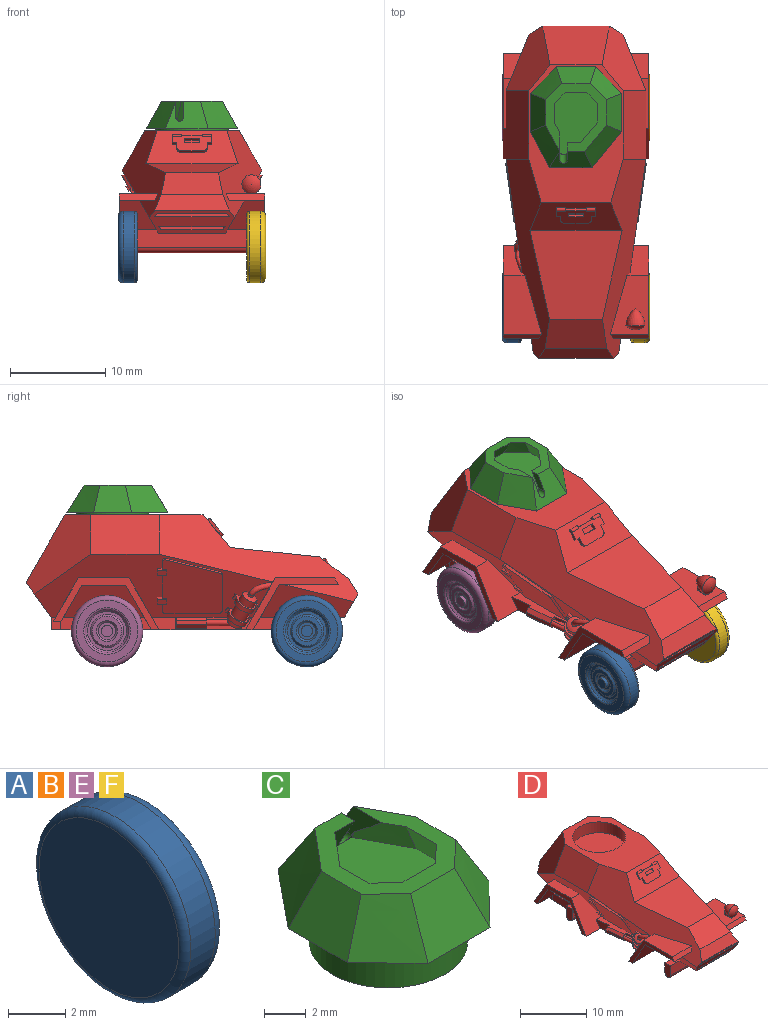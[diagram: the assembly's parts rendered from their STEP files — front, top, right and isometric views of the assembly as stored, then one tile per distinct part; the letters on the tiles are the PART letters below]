
ASSEMBLY  parts=6 mates=5
PART A: 14 faces, bbox 2x8.1x8.1 mm
  f0: cone r=1.75mm half-angle=45deg, axis (-1,0,0), area 2.9mm2, adj f1,f13
  f1: plane 3.1x3.1mm, normal (1,0,0), area 3.7mm2, adj f0,f2
  f2: cone r=0.9mm half-angle=45deg, axis (1,0,0), area 1.8mm2, adj f1,f3
  f3: plane 1.8x1.8mm, normal (1,0,0), area 1.4mm2, adj f2,f4
  f4: cylinder r=0.6mm len=1.2mm, axis (-1,0,0), area 1.5mm2, adj f3,f5
  f5: plane 1.2x1.2mm, normal (1,0,0), area 1.1mm2, adj f4
  f6: plane 6.9x6.9mm, normal (-1,0,0), area 37.4mm2, adj f7
  f7: torus R=3.45mm, axis (-1,0,0), area 10.8mm2, adj f6,f8
  f8: cylinder r=3.75mm len=7.5mm, axis (-1,0,0), area 28.3mm2, adj f7,f9
  f9: torus R=3.25mm, axis (-1,0,0), area 17.6mm2, adj f8,f10
  f10: plane 6.5x6.5mm, normal (1,0,0), area 14.3mm2, adj f9,f11
  f11: torus R=2.45mm, axis (-1,0,0), area 4.6mm2, adj f10,f12
  f12: cone r=2.25mm half-angle=45deg, axis (1,0,0), area 3.8mm2, adj f11,f13
  f13: plane 4.1x4.1mm, normal (1,0,0), area 3.6mm2, adj f0,f12
PART B: same geometry as A
PART C: 25 faces, bbox 11.2x12.2x7.1 mm
  f0: plane 4.5x2.9mm, normal (0,0.86,0.51), area 10.1mm2, adj f3,f4,f7,f8,f20,f21,f22
  f1: plane 0.63x0.61mm, normal (0,-0.86,-0.51), area 0.1mm2, adj f12,f15,f20,f22
  f2: plane 2.35x2.11mm, normal (0,-0.86,-0.51), area 4.1mm2, adj f4,f12,f16,f21,f22
  f3: plane 10.6x9.6mm, normal (0,0,-1), area 39.1mm2, adj f0,f5,f6,f7,f8,f9,f10,f11
  f4: plane 7.1x6.4mm, normal (0,0,1), area 16.9mm2, adj f0,f2,f5,f6,f7,f8,f9,f10
  f5: bspline ~3.54x3.39mm, area 10.4mm2, adj f3,f4,f6,f11
  f6: plane 4x2.9mm, normal (0.88,0,0.48), area 11.1mm2, adj f3,f4,f5,f7
  f7: bspline ~4.55x3.33mm, area 12.6mm2, adj f0,f3,f4,f6
  f8: bspline ~4.54x4.02mm, area 14.2mm2, adj f0,f3,f4,f9
  f9: plane 4x2.9mm, normal (-0.88,0,0.48), area 11.1mm2, adj f3,f4,f8,f10
  f10: bspline ~3.54x3.39mm, area 10.4mm2, adj f3,f4,f9,f11
  f11: plane 4.2x2.9mm, normal (0,-0.85,0.53), area 12.3mm2, adj f3,f4,f5,f10
  f12: plane 7.77x6.89mm, normal (0,0,1), area 44.2mm2, adj f1,f2,f13,f14,f15,f16,f17,f18
  f13: offset ~5.14x4.99mm, area 5.1mm2, adj f4,f12,f14,f19
  f14: plane 3.04x2.13mm, normal (-0.88,0,-0.48), area 6.1mm2, adj f4,f12,f13,f15
  f15: offset ~6.15x4.93mm, area 5.8mm2, adj f1,f4,f12,f14,f20
  f16: offset ~6.14x5.62mm, area 8mm2, adj f2,f4,f12,f17
  f17: plane 2.96x2.13mm, normal (0.88,0,-0.48), area 5.9mm2, adj f4,f12,f16,f18
  f18: offset ~5.14x4.99mm, area 5.1mm2, adj f4,f12,f17,f19
  f19: plane 3.14x2.12mm, normal (0,0.85,-0.53), area 6.7mm2, adj f4,f12,f13,f18
  f20: plane 2.95x1.7mm, normal (-1,0,0), area 2.3mm2, adj f0,f1,f4,f15,f22
  f21: plane 1.92x1.7mm, normal (1,0,0), area 1.6mm2, adj f0,f2,f4,f22
  f22: cylinder r=0.4mm len=1.16mm, axis (0,1,0), area 1.2mm2, adj f0,f1,f2,f20,f21
  f23: cylinder r=3.8mm len=7.6mm, axis (0,0,1), area 52.5mm2, adj f3,f24
  f24: plane 7.6x7.6mm, normal (0,0,-1), area 45.4mm2, adj f23
PART D: 210 faces, bbox 15.4x35x12.9 mm
  f0: plane 10.64x1.33mm, normal (-0.99,-0.11,0), area 5.7mm2, adj f1,f2,f5,f14,f104,f109,f137,f177
  f1: cylinder r=0.86mm len=1.76mm, axis (0.45,0.45,-0.77), area 2.1mm2, adj f0,f2,f3,f6,f137,f172,f178,f198
  f2: plane 1.59x1.31mm, normal (0.45,0.45,-0.77), area 0.9mm2, adj f0,f1,f198,f199,f201
  f3: plane 25.09x6.62mm, normal (-0.87,0,-0.5), area 73.1mm2, adj f1,f4,f5,f32,f95,f99,f100,f101
  f4: cylinder r=0.86mm len=2.12mm, axis (0.45,0.45,-0.77), area 6.7mm2, adj f3,f177,f186
  f5: plane 0.33x0.04mm, normal (0,0,1), area 0mm2, adj f0,f3,f177
  f6: plane 2.66x0.3mm, normal (-0.99,-0.11,0), area 0.7mm2, adj f1,f137,f172,f196,f200
  f7: plane 6.2x4.05mm, normal (0,0,1), area 18.4mm2, adj f25,f36,f37,f38,f165,f166,f167,f168
  f8: plane 9.67x3.45mm, normal (0,-0.77,0.64), area 30.3mm2, adj f9,f25,f26,f27,f99,f144,f145,f146
  f9: plane 2.2x0.23mm, normal (0,0.64,0.77), area 0.7mm2, adj f8,f157,f160,f161
  f10: plane 9.16x5.26mm, normal (0,0,-1), area 47.4mm2, adj f12,f64,f68,f86,f90,f133
  f11: plane 3.98x1.04mm, normal (0,0,1), area 3.9mm2, adj f12,f18,f22,f86
  f12: plane 4.25x1.33mm, normal (1,0.03,0), area 5.6mm2, adj f10,f11,f18,f64,f86
  f13: plane 4.28x1.47mm, normal (0,0,-1), area 5.4mm2, adj f15,f23,f34,f81
  f14: plane 19.8x15.3mm, normal (0,0,-1), area 161.2mm2, adj f0,f15,f17,f34,f36,f38,f40,f42
  f15: plane 5.05x1.33mm, normal (1,-0.1,0), area 6.2mm2, adj f13,f14,f34,f81
  f16: plane 8.96x2.43mm, normal (0,-0.87,-0.5), area 17mm2, adj f23,f24,f25,f29,f71,f72,f73,f75
  f17: plane 4.66x4.11mm, normal (0,0.87,-0.5), area 16.6mm2, adj f14,f22,f41,f42,f66,f67
  f18: plane 4.11x3.79mm, normal (0,-0.87,-0.5), area 13.8mm2, adj f11,f12,f20,f22,f41,f42
  f19: plane 4.59x4.11mm, normal (0,0.87,0.5), area 15.6mm2, adj f20,f21,f39,f42,f64,f65
  f20: plane 3.2x0.8mm, normal (0,0,-1), area 2.6mm2, adj f18,f19,f42,f64
  f21: plane 25.07x6.6mm, normal (0.87,0,-0.5), area 76.5mm2, adj f19,f25,f30,f32,f33,f36,f39,f40
  f22: plane 8.46x3.33mm, normal (0.87,0,-0.5), area 24.7mm2, adj f11,f17,f18,f41,f66,f84,f85,f86
  f23: plane 9.79x3.43mm, normal (0.87,0,-0.5), area 25.8mm2, adj f13,f16,f24,f25,f34,f35,f79,f80
  f24: plane 7.08x3.37mm, normal (0,0,-1), area 23.9mm2, adj f16,f23,f79,f98
  f25: plane 20.88x9.13mm, normal (0.84,-0.24,0.49), area 81.9mm2, adj f7,f8,f16,f21,f23,f26,f27,f28
  f26: plane 14.5x9.9mm, normal (0,0,1), area 81.4mm2, adj f8,f25,f30,f31,f33,f99,f100,f101
  f27: plane 9.67x9.35mm, normal (0,-0.1,0.99), area 71.5mm2, adj f8,f25,f28,f99
  f28: plane 6.49x3.04mm, normal (0,-0.6,0.8), area 22.9mm2, adj f25,f27,f29,f99
  f29: plane 7.78x1.61mm, normal (0,-0.85,0.53), area 13.6mm2, adj f16,f25,f28,f99
  f30: plane 7.2x4.16mm, normal (0.87,0,0.5), area 34.6mm2, adj f21,f25,f26,f33
  f31: plane 7.1x6.99mm, normal (0,0.87,0.5), area 51.2mm2, adj f26,f32,f33,f101
  f32: plane 9.88x3.65mm, normal (0,0.81,-0.59), area 38.2mm2, adj f3,f21,f31,f33,f68,f101
  f33: plane 8.33x6.8mm, normal (0.71,0.58,0.41), area 41.3mm2, adj f21,f26,f30,f31,f32
  f34: plane 5.15x4.76mm, normal (0,-0.87,-0.5), area 20.2mm2, adj f13,f14,f15,f23,f35,f38
  f35: plane 6.2x3.76mm, normal (0,0,-1), area 17.9mm2, adj f23,f25,f34,f37,f38
  f36: plane 5.46x4.11mm, normal (0,0.87,0.5), area 20.3mm2, adj f7,f14,f21,f25,f38,f70
  f37: plane 4.05x0.69mm, normal (0,-0.87,0.5), area 3.1mm2, adj f7,f25,f35,f38
  f38: plane 9.75x5.46mm, normal (1,0,0), area 8.4mm2, adj f7,f14,f34,f35,f36,f37
  f39: plane 5.3x1.73mm, normal (0,0,1), area 9.1mm2, adj f19,f21,f40,f42
  f40: plane 5.46x4.11mm, normal (0,-0.87,0.5), area 18.4mm2, adj f14,f21,f39,f42,f69,f70
  f41: plane 4.62x2.19mm, normal (0,0,-1), area 10.1mm2, adj f17,f18,f22,f42
  f42: plane 11.1x5.46mm, normal (1,0,0), area 11.4mm2, adj f14,f17,f18,f19,f20,f39,f40,f41
  f43: plane 2.67x1.71mm, normal (0,1,0), area 0.9mm2, adj f21,f53,f55,f60
  f44: plane 0.93x0.71mm, normal (0,1,0), area 0.3mm2, adj f21,f45,f53,f54
  f45: cylinder r=0.3mm len=0.41mm, axis (-0.87,0,0.5), area 0.2mm2, adj f21,f44,f46,f53
  f46: plane 5.7x1.54mm, normal (0.48,-0.27,0.83), area 1.8mm2, adj f21,f45,f47,f53
  f47: cylinder r=0.3mm len=0.4mm, axis (-0.87,0,0.5), area 0.1mm2, adj f21,f46,f48,f53
  f48: plane 3.88x2.41mm, normal (0,-1,0), area 1.3mm2, adj f21,f47,f49,f53
  f49: cylinder r=0.3mm len=0.41mm, axis (-0.87,0,0.5), area 0.1mm2, adj f21,f48,f50,f53
  f50: plane 5.7x0.26mm, normal (-0.5,0,-0.87), area 1.7mm2, adj f21,f49,f51,f53
  f51: cylinder r=0.3mm len=0.41mm, axis (-0.87,0,0.5), area 0.1mm2, adj f21,f50,f52,f53
  f52: plane 0.93x0.71mm, normal (0,1,0), area 0.3mm2, adj f21,f51,f53,f59
  f53: plane 6.3x5.63mm, normal (0.87,0,-0.5), area 35.3mm2, adj f43,f44,f45,f46,f47,f48,f49,f50
  f54: plane 1x0.43mm, normal (0.5,0,0.87), area 0.4mm2, adj f21,f44,f53,f56,f57,f58
  f55: plane 1x0.43mm, normal (-0.5,0,-0.87), area 0.4mm2, adj f21,f43,f53,f56,f57,f58
  f56: plane 0.62x0.47mm, normal (0,-1,0), area 0.1mm2, adj f53,f54,f55,f58
  f57: plane 0.77x0.73mm, normal (0,1,0), area 0.3mm2, adj f21,f54,f55,f58
  f58: plane 1x0.52mm, normal (0.87,0,-0.5), area 0.6mm2, adj f54,f55,f56,f57
  f59: plane 1x0.43mm, normal (-0.5,0,-0.87), area 0.3mm2, adj f21,f52,f53,f61,f62,f63
  f60: plane 1x0.43mm, normal (0.5,0,0.87), area 0.3mm2, adj f21,f43,f53,f61,f62,f63
  f61: plane 0.77x0.73mm, normal (0,1,0), area 0.3mm2, adj f21,f59,f60,f63
  f62: plane 0.62x0.47mm, normal (0,-1,0), area 0.1mm2, adj f53,f59,f60,f63
  f63: plane 1x0.52mm, normal (0.87,0,-0.5), area 0.6mm2, adj f59,f60,f61,f62
  f64: plane 1.33x1.01mm, normal (1,0,0), area 1mm2, adj f10,f12,f19,f20,f65,f68
  f65: plane 0.91x0.48mm, normal (0,0,1), area 0.4mm2, adj f19,f21,f64,f68
  f66: plane 3.28x1.18mm, normal (0,0,1), area 3.7mm2, adj f17,f22,f67,f85
  f67: plane 4.05x1.33mm, normal (1,0.03,0), area 4.9mm2, adj f14,f17,f66,f85
  f68: plane 8.9x1.33mm, normal (0,1,0), area 11.8mm2, adj f10,f32,f64,f65,f133,f134
  f69: plane 10.64x1.2mm, normal (0,0,1), area 6.4mm2, adj f21,f40,f70
  f70: plane 10.64x1.33mm, normal (0.99,-0.11,0), area 13.2mm2, adj f14,f36,f40,f69
  f71: plane 6.59x0.52mm, normal (0,-0.5,0.87), area 4mm2, adj f16,f72,f74,f138
  f72: plane 0.72x0.65mm, normal (-0.89,-0.22,0.39), area 0.3mm2, adj f16,f71,f73,f74
  f73: plane 6.99x0.52mm, normal (0,0.5,-0.87), area 4.2mm2, adj f16,f72,f74,f138
  f74: plane 6.99x0.35mm, normal (0,-0.87,-0.5), area 2.7mm2, adj f71,f72,f73,f138
  f75: plane 0.72x0.65mm, normal (-0.84,0.27,-0.47), area 0.3mm2, adj f16,f76,f77,f78
  f76: plane 7.34x0.52mm, normal (0,0.5,-0.87), area 4.4mm2, adj f16,f75,f78,f139
  f77: plane 7.86x0.52mm, normal (0,-0.5,0.87), area 4.7mm2, adj f16,f75,f78,f139
  f78: plane 7.86x0.35mm, normal (0,-0.87,-0.5), area 3mm2, adj f75,f76,f77,f139
  f79: plane 11.5x1.8mm, normal (0,-1,0), area 18.3mm2, adj f23,f24,f80,f82,f83,f98,f140,f141
  f80: plane 2.02x1.2mm, normal (0,0,1), area 2.4mm2, adj f23,f79,f81,f83
  f81: plane 11.5x1.8mm, normal (0,1,0), area 12.8mm2, adj f13,f14,f15,f23,f80,f82,f83,f91
  f82: cylinder r=0.6mm len=11.5mm, axis (-1,0,0), area 21.7mm2, adj f79,f81,f83,f141
  f83: plane 2.4x1.2mm, normal (1,0,0), area 2.7mm2, adj f79,f80,f81,f82
  f84: plane 2.02x1.2mm, normal (0,0,1), area 2.4mm2, adj f22,f85,f86,f88
  f85: plane 11.5x1.8mm, normal (0,-1,0), area 6mm2, adj f14,f22,f66,f67,f84,f87,f88,f97
  f86: plane 11.5x1.8mm, normal (0,1,0), area 6.1mm2, adj f10,f11,f12,f22,f84,f87,f88,f89
  f87: cylinder r=0.6mm len=11.5mm, axis (-1,0,0), area 21.7mm2, adj f85,f86,f88,f143
  f88: plane 2.4x1.2mm, normal (1,0,0), area 2.7mm2, adj f84,f85,f86,f87
  f89: plane 3.98x1.04mm, normal (0,0,1), area 3.9mm2, adj f86,f90,f94,f97
  f90: plane 4.25x1.33mm, normal (-1,0.03,0), area 5.6mm2, adj f10,f86,f89,f94,f133
  f91: plane 4.28x1.47mm, normal (0,0,-1), area 5.4mm2, adj f81,f92,f98,f102
  f92: plane 5.05x1.33mm, normal (-1,-0.1,0), area 6.2mm2, adj f14,f81,f91,f102
  f93: plane 4.66x4.11mm, normal (0,0.87,-0.5), area 16.6mm2, adj f14,f97,f110,f111,f135,f136
  f94: plane 4.11x3.79mm, normal (0,-0.87,-0.5), area 13.8mm2, adj f89,f90,f96,f97,f110,f111
  f95: plane 4.59x4.11mm, normal (0,0.87,0.5), area 15.6mm2, adj f3,f96,f108,f111,f133,f134
  f96: plane 3.2x0.8mm, normal (0,0,-1), area 2.6mm2, adj f94,f95,f111,f133
  f97: plane 8.46x3.33mm, normal (-0.87,0,-0.5), area 24.7mm2, adj f85,f86,f89,f93,f94,f110,f135,f142
  f98: plane 9.79x3.43mm, normal (-0.87,0,-0.5), area 25.8mm2, adj f16,f24,f79,f81,f91,f99,f102,f103
  f99: plane 20.88x9.13mm, normal (-0.84,-0.24,0.49), area 81.9mm2, adj f3,f8,f16,f26,f27,f28,f29,f98
  f100: plane 7.2x4.16mm, normal (-0.87,0,0.5), area 34.6mm2, adj f3,f26,f99,f101
  f101: plane 8.33x6.8mm, normal (-0.71,0.58,0.41), area 41.3mm2, adj f3,f26,f31,f32,f100
  f102: plane 5.15x4.76mm, normal (0,-0.87,-0.5), area 20.2mm2, adj f14,f91,f92,f98,f103,f107
  f103: plane 6.2x3.76mm, normal (0,0,-1), area 17.9mm2, adj f98,f99,f102,f105,f107
  f104: plane 5.49x4.14mm, normal (0,0.87,0.5), area 20.1mm2, adj f0,f3,f14,f99,f106,f107,f192,f193
  f105: plane 4.05x0.69mm, normal (0,-0.87,0.5), area 3.1mm2, adj f99,f103,f106,f107
  f106: plane 6.2x4.05mm, normal (0,0,1), area 19.7mm2, adj f99,f104,f105,f107
  f107: plane 9.75x5.46mm, normal (-1,0,0), area 8.4mm2, adj f14,f102,f103,f104,f105,f106
  f108: plane 5.3x1.73mm, normal (0,0,1), area 9.1mm2, adj f3,f95,f109,f111
  f109: plane 5.46x4.11mm, normal (0,-0.87,0.5), area 18.4mm2, adj f0,f3,f14,f108,f111,f137
  f110: plane 4.62x2.19mm, normal (0,0,-1), area 10.1mm2, adj f93,f94,f97,f111
  f111: plane 11.1x5.46mm, normal (-1,0,0), area 11.4mm2, adj f14,f93,f94,f95,f96,f108,f109,f110
  f112: plane 2.67x1.71mm, normal (0,1,0), area 0.9mm2, adj f3,f122,f124,f129
  f113: plane 0.93x0.71mm, normal (0,1,0), area 0.3mm2, adj f3,f114,f122,f123
  f114: cylinder r=0.3mm len=0.41mm, axis (0.87,0,0.5), area 0.2mm2, adj f3,f113,f115,f122
  f115: plane 5.7x1.54mm, normal (-0.48,-0.27,0.83), area 1.8mm2, adj f3,f114,f116,f122
  f116: cylinder r=0.3mm len=0.4mm, axis (0.87,0,0.5), area 0.1mm2, adj f3,f115,f117,f122
  f117: plane 3.88x2.41mm, normal (0,-1,0), area 1.3mm2, adj f3,f116,f118,f122
  f118: cylinder r=0.3mm len=0.41mm, axis (0.87,0,0.5), area 0.1mm2, adj f3,f117,f119,f122
  f119: plane 5.7x0.26mm, normal (0.5,0,-0.87), area 1.7mm2, adj f3,f118,f120,f122
  f120: cylinder r=0.3mm len=0.41mm, axis (0.87,0,0.5), area 0.1mm2, adj f3,f119,f121,f122
  f121: plane 0.93x0.71mm, normal (0,1,0), area 0.3mm2, adj f3,f120,f122,f128
  f122: plane 6.3x5.63mm, normal (-0.87,0,-0.5), area 35.3mm2, adj f112,f113,f114,f115,f116,f117,f118,f119
  f123: plane 1x0.43mm, normal (-0.5,0,0.87), area 0.4mm2, adj f3,f113,f122,f125,f126,f127
  f124: plane 1x0.43mm, normal (0.5,0,-0.87), area 0.4mm2, adj f3,f112,f122,f125,f126,f127
  f125: plane 0.62x0.47mm, normal (0,-1,0), area 0.1mm2, adj f122,f123,f124,f127
  f126: plane 0.77x0.73mm, normal (0,1,0), area 0.3mm2, adj f3,f123,f124,f127
  f127: plane 1x0.52mm, normal (-0.87,0,-0.5), area 0.6mm2, adj f123,f124,f125,f126
  f128: plane 1x0.43mm, normal (0.5,0,-0.87), area 0.3mm2, adj f3,f121,f122,f130,f131,f132
  f129: plane 1x0.43mm, normal (-0.5,0,0.87), area 0.3mm2, adj f3,f112,f122,f130,f131,f132
  f130: plane 0.77x0.73mm, normal (0,1,0), area 0.3mm2, adj f3,f128,f129,f132
  f131: plane 0.62x0.47mm, normal (0,-1,0), area 0.1mm2, adj f122,f128,f129,f132
  f132: plane 1x0.52mm, normal (-0.87,0,-0.5), area 0.6mm2, adj f128,f129,f130,f131
  f133: plane 1.33x1.01mm, normal (-1,0,0), area 1mm2, adj f10,f68,f90,f95,f96,f134
  f134: plane 0.91x0.48mm, normal (0,0,1), area 0.4mm2, adj f3,f68,f95,f133
  f135: plane 3.28x1.18mm, normal (0,0,1), area 3.7mm2, adj f85,f93,f97,f136
  f136: plane 4.05x1.33mm, normal (-1,0.03,0), area 4.9mm2, adj f14,f85,f93,f135
  f137: plane 8.7x1.31mm, normal (0,0,1), area 7.4mm2, adj f0,f1,f3,f6,f109,f196,f197,f203
  f138: plane 0.72x0.65mm, normal (0.89,-0.22,0.39), area 0.3mm2, adj f16,f71,f73,f74
  f139: plane 0.72x0.65mm, normal (0.84,0.27,-0.47), area 0.3mm2, adj f16,f76,f77,f78
  f140: plane 2.02x1.2mm, normal (0,0,1), area 2.4mm2, adj f79,f81,f98,f141
  f141: plane 2.4x1.2mm, normal (-1,0,0), area 2.7mm2, adj f79,f81,f82,f140
  f142: plane 2.02x1.2mm, normal (0,0,1), area 2.4mm2, adj f85,f86,f97,f143
  f143: plane 2.4x1.2mm, normal (-1,0,0), area 2.7mm2, adj f85,f86,f87,f142
  f144: plane 0.5x0.23mm, normal (0,-0.64,-0.77), area 0.2mm2, adj f8,f145,f156,f157
  f145: plane 0.65x0.62mm, normal (-1,0,0), area 0.2mm2, adj f8,f144,f146,f157
  f146: cylinder r=0.5mm len=0.58mm, axis (0,0.77,-0.64), area 0.2mm2, adj f8,f145,f147,f157
  f147: plane 2.2x0.23mm, normal (0,-0.64,-0.77), area 0.7mm2, adj f8,f146,f148,f157
  f148: cylinder r=0.5mm len=0.58mm, axis (0,0.77,-0.64), area 0.2mm2, adj f8,f147,f149,f157
  f149: plane 0.65x0.62mm, normal (1,0,0), area 0.2mm2, adj f8,f148,f150,f157
  f150: plane 0.5x0.23mm, normal (0,-0.64,-0.77), area 0.2mm2, adj f8,f149,f151,f157
  f151: plane 1.06x0.96mm, normal (1,0,0), area 0.4mm2, adj f8,f150,f157,f162
  f152: plane 0.65x0.62mm, normal (1,0,0), area 0.2mm2, adj f153,f155,f157,f158
  f153: plane 1.5x0.23mm, normal (0,-0.64,-0.77), area 0.5mm2, adj f152,f154,f157,f158
  f154: plane 0.65x0.62mm, normal (-1,0,0), area 0.2mm2, adj f153,f155,f157,f158
  f155: plane 1.5x0.23mm, normal (0,0.64,0.77), area 0.5mm2, adj f152,f154,f157,f158
  f156: plane 1.06x0.96mm, normal (-1,0,0), area 0.4mm2, adj f8,f144,f157,f159
  f157: plane 4.2x1.61mm, normal (0,-0.77,0.64), area 6.4mm2, adj f9,f144,f145,f146,f147,f148,f149,f150
  f158: plane 1.5x0.46mm, normal (0,-0.77,0.64), area 0.9mm2, adj f152,f153,f154,f155
  f159: cylinder r=0.2mm len=1mm, axis (-1,0,0), area 0.6mm2, adj f8,f156,f157,f160
  f160: plane 0.4x0.3mm, normal (1,0,0), area 0.1mm2, adj f8,f9,f157,f159
  f161: plane 0.4x0.3mm, normal (-1,0,0), area 0.1mm2, adj f8,f9,f157,f162
  f162: cylinder r=0.2mm len=1mm, axis (-1,0,0), area 0.6mm2, adj f8,f151,f157,f161
  f163: revolved ~2x2mm, area 7.3mm2, adj f164,f167,f168,f169
  f164: sphere r=1.45mm, area 3.6mm2, adj f163,f165,f166
  f165: plane 0.5x0.13mm, normal (0,-1,0), area 0mm2, adj f7,f164,f167
  f166: plane 0.5x0.13mm, normal (0,-1,0), area 0mm2, adj f7,f164,f169
  f167: plane 1.3x0.76mm, normal (1,0,0), area 0.4mm2, adj f7,f163,f165,f168
  f168: plane 1x0.76mm, normal (0,1,0), area 0.5mm2, adj f7,f163,f167,f169
  f169: plane 1.3x0.76mm, normal (-1,0,0), area 0.4mm2, adj f7,f163,f166,f168
  f170: sphere r=1.95mm, area 2.2mm2, adj f3,f171,f173
  f171: cylinder r=0.86mm len=1.9mm, axis (0.45,0.45,-0.77), area 4.1mm2, adj f3,f170,f185
  f172: plane 0.43x0.43mm, normal (0.45,0.45,-0.77), area 0.1mm2, adj f1,f6,f200
  f173: cylinder r=0.3mm len=0.64mm, axis (0.45,0.45,-0.77), area 0.4mm2, adj f170,f193
  f174: plane 0.48x0.45mm, normal (-0.87,0,-0.5), area 0.1mm2, adj f175,f177,f178,f182
  f175: plane 0.74x0.69mm, normal (-0.22,0.89,0.39), area 0.3mm2, adj f174,f176,f177,f178
  f176: cylinder r=1.1mm len=2.19mm, axis (0.45,0.45,-0.77), area 1.7mm2, adj f175,f177,f178,f179
  f177: plane 2.42x2.02mm, normal (-0.45,-0.45,0.77), area 1.6mm2, adj f0,f3,f4,f5,f174,f175,f176,f179
  f178: plane 2.19x1.71mm, normal (0.45,0.45,-0.77), area 1.3mm2, adj f0,f1,f3,f174,f175,f176,f179,f182
  f179: plane 0.71x0.69mm, normal (0.22,-0.89,-0.39), area 0.3mm2, adj f0,f176,f177,f178,f180
  f180: plane 0.41x0.38mm, normal (-0.87,0,-0.5), area 0.1mm2, adj f0,f177,f179,f181
  f181: plane 0.39x0.18mm, normal (0.22,-0.89,-0.39), area 0mm2, adj f0,f177,f180
  f182: plane 0.51x0.44mm, normal (-0.22,0.89,0.39), area 0.1mm2, adj f3,f174,f177,f178
  f183: plane 0.51x0.44mm, normal (0.22,-0.89,-0.39), area 0.1mm2, adj f3,f185,f186,f187
  f184: plane 0.51x0.44mm, normal (-0.22,0.89,0.39), area 0.1mm2, adj f3,f185,f186,f191
  f185: plane 2.42x2.02mm, normal (-0.45,-0.45,0.77), area 1.6mm2, adj f3,f171,f183,f184,f187,f188,f189,f190
  f186: plane 2.42x2.02mm, normal (0.45,0.45,-0.77), area 1.6mm2, adj f3,f4,f183,f184,f187,f188,f189,f190
  f187: plane 0.48x0.45mm, normal (-0.87,0,-0.5), area 0.1mm2, adj f183,f185,f186,f188
  f188: plane 0.74x0.69mm, normal (0.22,-0.89,-0.39), area 0.3mm2, adj f185,f186,f187,f189
  f189: cylinder r=1.1mm len=2.19mm, axis (0.45,0.45,-0.77), area 1.7mm2, adj f185,f186,f188,f190
  f190: plane 0.74x0.69mm, normal (-0.22,0.89,0.39), area 0.3mm2, adj f185,f186,f189,f191
  f191: plane 0.48x0.45mm, normal (-0.87,0,-0.5), area 0.1mm2, adj f184,f185,f186,f190
  f192: plane 0.27x0.26mm, normal (0.4,-0.9,0.18), area 0mm2, adj f3,f104,f193
  f193: bspline ~2.49x1.44mm, area 4.2mm2, adj f3,f104,f173,f192
  f194: plane 3.18x0.4mm, normal (-0.99,-0.11,0), area 1.3mm2, adj f196,f197,f202,f203
  f195: plane 3.22x0.76mm, normal (0,0,-1), area 1.3mm2, adj f0,f196,f197,f202
  f196: plane 1.2x0.8mm, normal (0.11,-0.99,0), area 0.4mm2, adj f0,f6,f137,f194,f195,f198,f199,f200
  f197: plane 1.2x0.8mm, normal (-0.11,0.99,0), area 0.8mm2, adj f0,f137,f194,f195,f202,f203
  f198: cylinder r=0.3mm len=3.36mm, axis (-0.11,0.99,0), area 2.4mm2, adj f1,f2,f196,f199,f200
  f199: plane 3.6x0.8mm, normal (0,0,-1), area 1.4mm2, adj f0,f2,f196,f198,f201
  f200: plane 2.66x0.7mm, normal (0,0,1), area 1mm2, adj f1,f6,f172,f196,f198
  f201: plane 0.2x0.13mm, normal (0.11,-0.99,0), area 0mm2, adj f0,f2,f199
  f202: plane 3.22x0.76mm, normal (-0.7,-0.08,-0.71), area 1.8mm2, adj f194,f195,f196,f197
  f203: plane 3.22x0.76mm, normal (-0.7,-0.08,0.71), area 1.8mm2, adj f137,f194,f196,f197
  f204: cylinder r=4mm len=8mm, axis (0,0,1), area 50.3mm2, adj f26,f205
  f205: plane 8x8mm, normal (0,0,1), area 50.3mm2, adj f204
  f206: plane 0.23x0.08mm, normal (-0.87,0,-0.5), area 0mm2, adj f207,f208,f209
  f207: plane 0.23x0.05mm, normal (0,0,1), area 0mm2, adj f206,f208,f209
  f208: cylinder r=0.86mm len=0.19mm, axis (0.45,0.45,-0.77), area 0mm2, adj f206,f207,f209
  f209: plane 0.18x0.08mm, normal (0.45,0.45,-0.77), area 0mm2, adj f206,f207,f208
PART E: same geometry as A
PART F: same geometry as A
PLACE A rot(axis=(0,-1,0.05),180deg) t=(-5.75,-24.22,-0.14)mm
PLACE B t=(5.75,-3.22,-0.14)mm
PLACE C rot(axis=(0,0,-1),180deg) t=(0,-3.8,12.28)mm
PLACE D t=(0,-13.3,-3.14)mm
PLACE E rot(axis=(0,1,0),180deg) t=(-5.75,-3.22,-0.14)mm
PLACE F t=(5.75,-24.22,-0.14)mm
MATE revolute C.f23 <-> D.f204  axis (0,0,-1) through (0,-3.8,10.08)mm
MATE revolute F.f0 <-> D.f82  axis (-1,0,0) through (5.75,-24.22,-0.14)mm
MATE revolute E.f0 <-> D.f87  axis (1,0,0) through (-5.75,-3.22,-0.14)mm
MATE revolute D.f87 <-> B.f0  axis (1,0,0) through (5.75,-3.22,-0.14)mm
MATE revolute A.f0 <-> D.f82  axis (1,0,0) through (-5.75,-24.22,-0.14)mm
